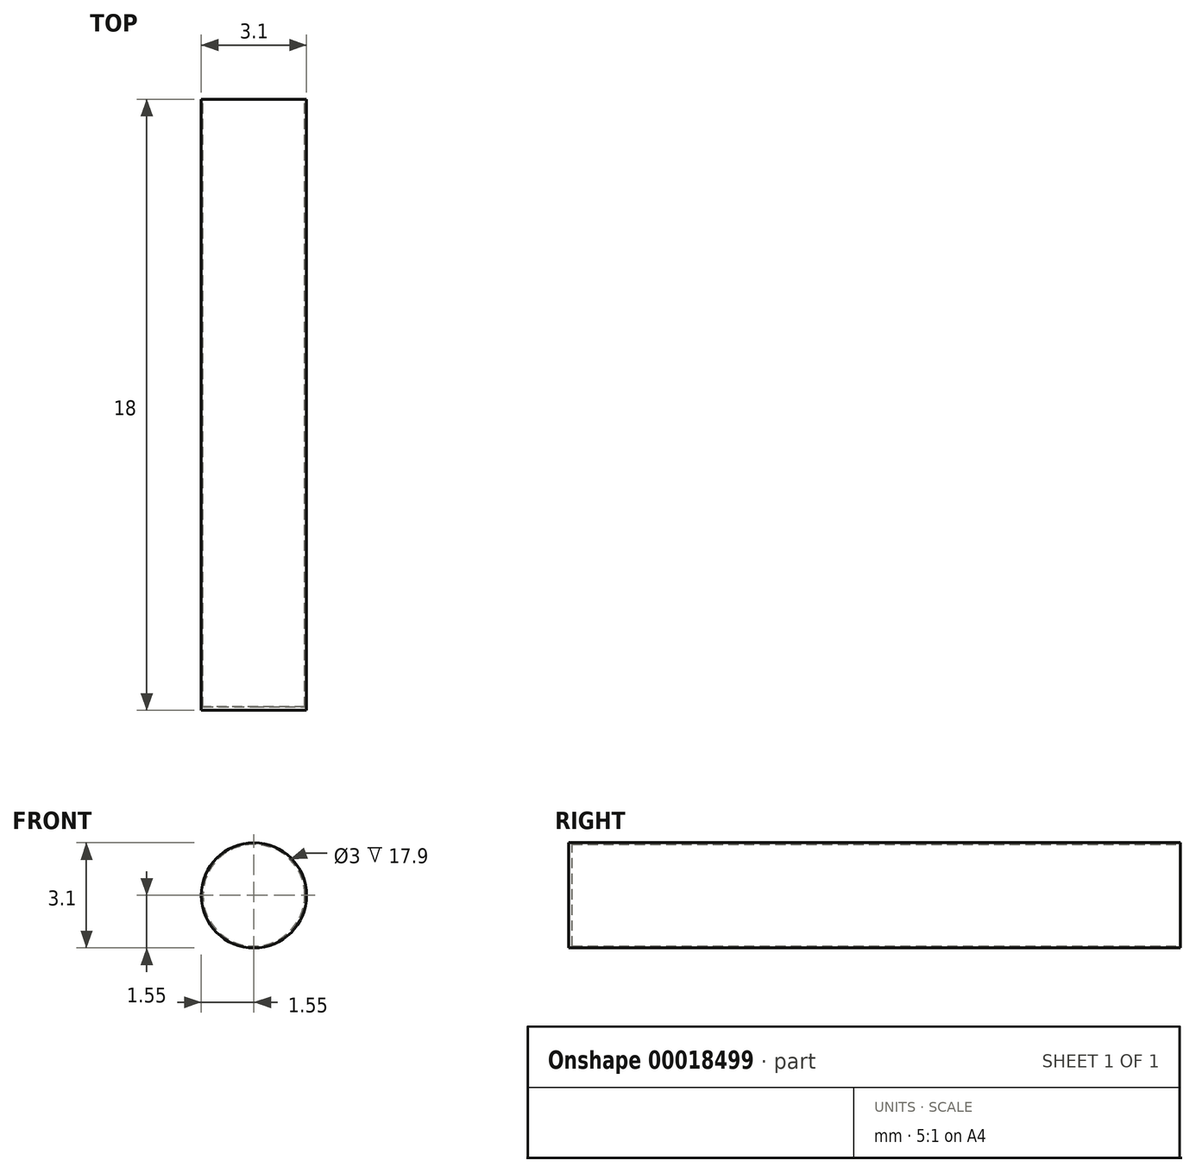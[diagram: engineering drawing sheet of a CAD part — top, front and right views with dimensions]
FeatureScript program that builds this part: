
annotation { "Feature Type Name" : "Feature", "Feature Type Description" : "" }
export const myFeature = defineFeature(function(context is Context, id is Id, definition is map)
    precondition{}
    {
        {
            var Q0;
            Q0=qCreatedBy(makeId("Front.planeOp"),FACE);
            var sketch = newSketch(context, id + "F0", { "sketchPlane" : qUnion([Q0])});
            skCircle(sketch, "E0", {"center": v(0, 0) * mm, "radius": 1.55 * mm});
            skSolve(sketch);
        }
        {
            var Q0;
            Q0=makeQuery(id+"F0.imprint","IMPRINT",FACE,{"disambiguationData":[TD([[makeQuery(id+"F0.imprint","IMPRINT",EDGE,{"derivedFrom":sQuery(id+"F0.wireOp",EDGE,"E0")}),1.0]])]});
            extrude(context, id + "F1", {"entities" : qUnion([Q0]), "depth" : 18 * mm});
        }
        {
            var Q0;
            Q0=makeQuery(id+"F0.imprint","IMPRINT",FACE,{"disambiguationData":[TD([[makeQuery(id+"F0.imprint","IMPRINT",EDGE,{"derivedFrom":sQuery(id+"F0.wireOp",EDGE,"E0")}),1.0]])]});
            var sketch = newSketch(context, id + "F2", { "sketchPlane" : qUnion([Q0])});
            skCircle(sketch, "E1", {"center": v(0, 0) * mm, "radius": 1.5 * mm});
            skSolve(sketch);
        }
        {
            var Q0;
            Q0=makeQuery(id+"F2.imprint","IMPRINT",FACE,{"disambiguationData":[TD([[makeQuery(id+"F2.imprint","IMPRINT",EDGE,{"derivedFrom":sQuery(id+"F2.wireOp",EDGE,"E1")}),1.0]])]});
            extrude(context, id + "F3", {"entities" : qUnion([Q0]), "operationType" : NewBodyOperationType.REMOVE, "depth" : 17.9 * mm});
        }
    });
